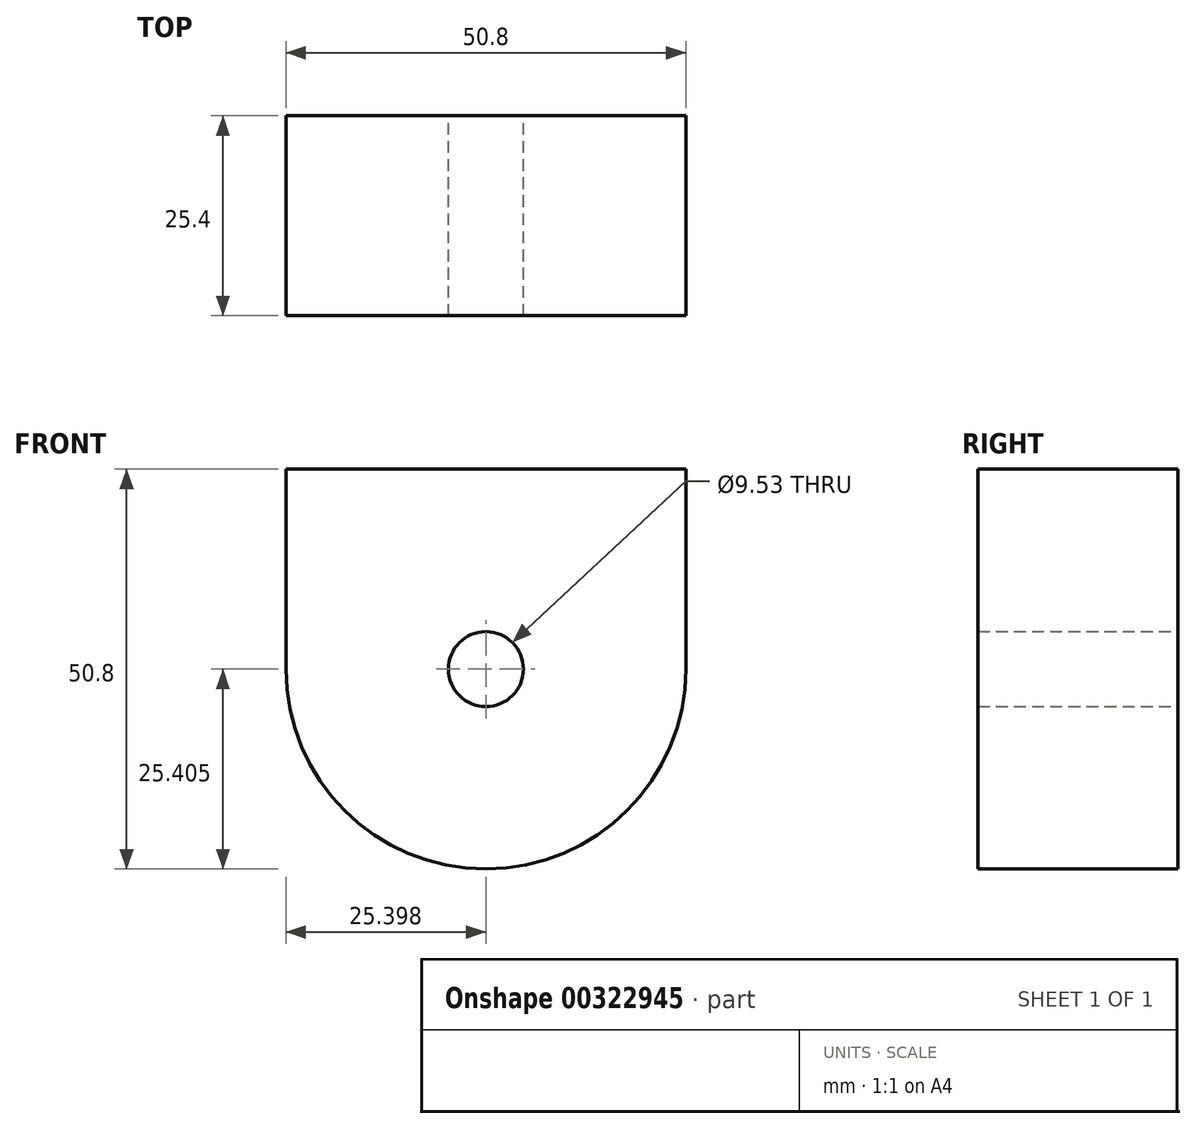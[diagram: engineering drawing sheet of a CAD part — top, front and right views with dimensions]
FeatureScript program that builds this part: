
annotation { "Feature Type Name" : "Feature", "Feature Type Description" : "" }
export const myFeature = defineFeature(function(context is Context, id is Id, definition is map)
    precondition{}
    {
        {
            var Q0;
            Q0=qCreatedBy(makeId("Front.planeOp"),FACE);
            var sketch = newSketch(context, id + "F0", { "sketchPlane" : qUnion([Q0])});
            skLineSegment(sketch, "E0", {"start": v(-72.61, 23.63) * mm, "end": v(-21.81, 23.63) * mm, "construction": true});
            skLineSegment(sketch, "E1", {"start": v(-21.81, 23.63) * mm, "end": v(-21.81, 49.03) * mm});
            skLineSegment(sketch, "E2", {"start": v(-72.61, 23.63) * mm, "end": v(-72.61, 49.03) * mm});
            skArc(sketch, "E3", {"start": v(-72.61, 23.63) * mm, "mid": v(-47.21, -1.77) * mm, "end": v(-21.81, 23.63) * mm});
            skLineSegment(sketch, "E4", {"start": v(-72.61, 49.03) * mm, "end": v(-21.81, 49.03) * mm});
            skCircle(sketch, "E5", {"center": v(-47.21, 23.63) * mm, "radius": 4.76 * mm});
            skSolve(sketch);
        }
        {
            var Q0;
            Q0 = qSketchRegion(id + "F0", true);
            extrude(context, id + "F1", {"entities" : qUnion([Q0]), "depth" : 25.4 * mm});
        }
    });
